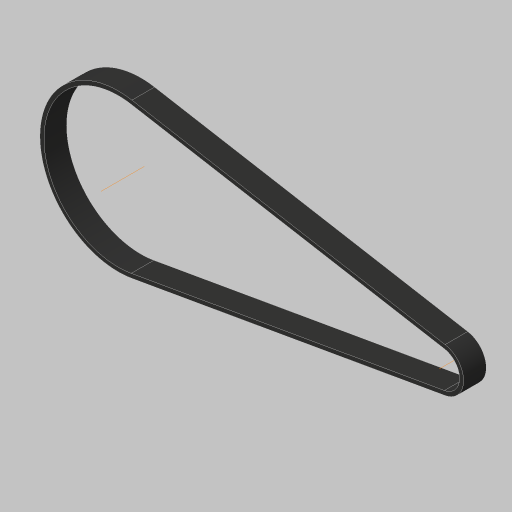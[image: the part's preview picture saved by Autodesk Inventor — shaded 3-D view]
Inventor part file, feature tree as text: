
AUTODESK INVENTOR PART (.ipt)
format: ipt  version: 2023.5 (Build 275446000, 446)  size: 165,376 bytes
history: native  units: in
note: dims shown in document units (in); Inventor stores cm internally (conversion verified against a paired STEP export)
features: sketch x3, extrude x1, other x1, projected_geometry x1
ambient origin geometry x8: Origin, YZ Plane, XZ Plane, XY Plane, X Axis, Y Axis, Z Axis, Center Point
bodies: Body1 (feature_tree)
feature tree (6):
  sketch  "Sketch2"  dims[d0=0.6015in d1=2.2558in]
  extrude  "Extrusion2"  Depth=2.2558in
  sketch  "Sketch5"  dims[d3=3.9365in d5=4.6983in d9=0.0787in d10=0.0598in d11=0.0299in d12=0.0219in d13=0.0219in d14=0.0059in d15=0.0059in d20=0.3346in d21=0.0in d22=0.0787in d23=0.0598in d24=0.0299in d25=0.0219in d26=0.0219in d27=0.0059in d28=0.0059in d29=0.0299in d30=0.0394in d31=0.0787in d32=0.0232in d34=0.0219in d35=0.0in d36=0.0in d37=0.0059in d38=0.0022in d39=0.0022in d40=0.0in d41=0.0in d42=0.0081in d43=0.0081in d44=0.0299in]
  other  "Work Axis1"
  sketch  "Sketch4"  dims[d2=0.8401in]
  projected_geometry  "Projected Loop1"
